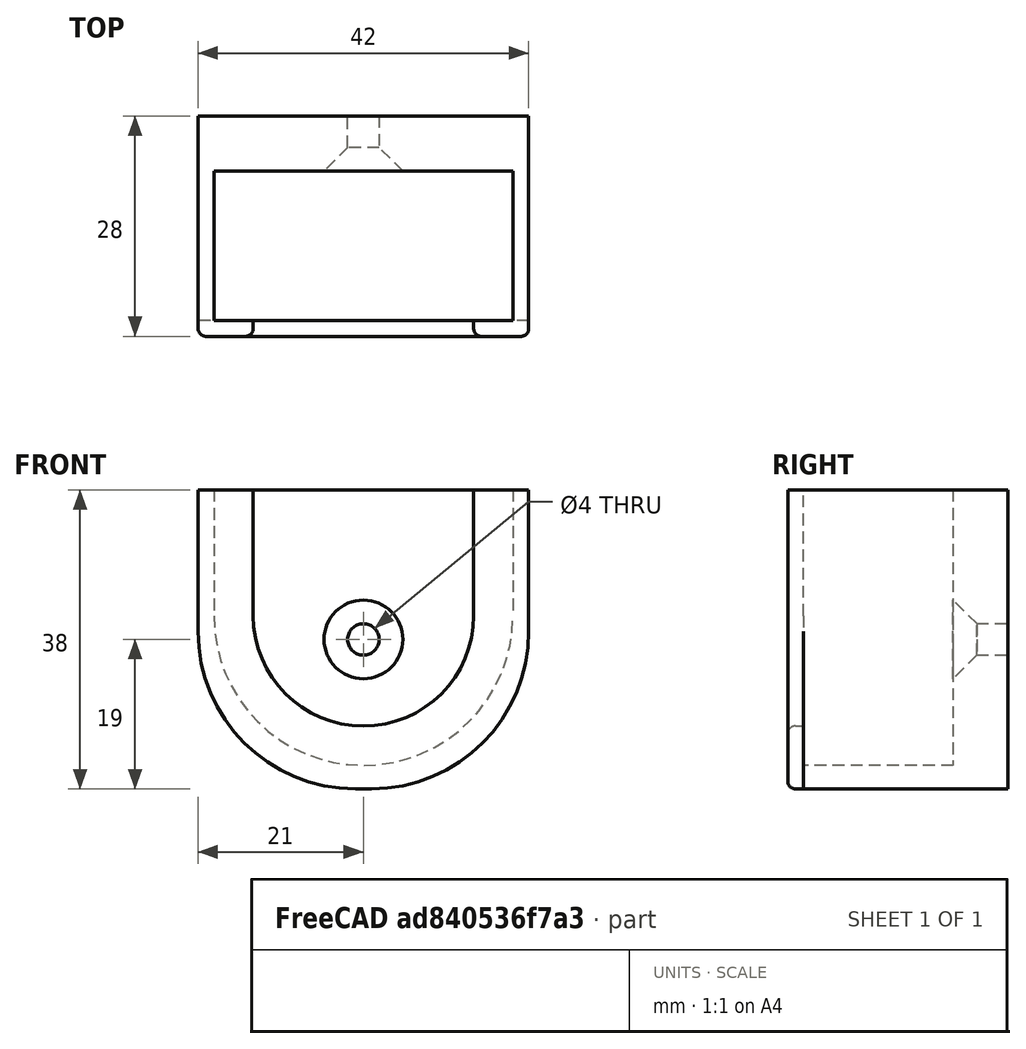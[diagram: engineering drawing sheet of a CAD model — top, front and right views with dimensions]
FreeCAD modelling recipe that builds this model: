
FCSTD DOCUMENT  (FreeCAD 0.19R24291 (Git))
Label: 003
License: All rights reserved
LicenseURL: http://en.wikipedia.org/wiki/All_rights_reserved
objects: PartDesign::Fillet×6, Sketcher::SketchObject×5, PartDesign::Pocket×3, PartDesign::Pad×2, PartDesign::Plane×1, PartDesign::Chamfer×1, PartDesign::Body×1
note: 31 computed .brp shape members not serialized (recipe doc carries the construction recipe); baked Part::Feature solids carry a one-line shape summary decoded from their .brp

FEATURE [Sketcher::SketchObject] Sketch
  FullyConstrained = true
  MapMode = 5
  Placement = pos=(0,0,0) rot=(1,0,0;1.5708rad)
  Support = -> [XZ_Plane]
  sketch-geometry (4):
    g0: LineSegment StartX=0 StartY=38 StartZ=0 EndX=42 EndY=38 EndZ=0
    g1: LineSegment StartX=42 StartY=38 StartZ=0 EndX=42 EndY=0 EndZ=0
    g2: LineSegment StartX=42 StartY=0 StartZ=0 EndX=0 EndY=0 EndZ=0
    g3: LineSegment StartX=0 StartY=0 StartZ=0 EndX=0 EndY=38 EndZ=0
  constraints (11):
    c: Coincident(g0,g1)
    c: Coincident(g1,g2)
    c: Coincident(g2,g3)
    c: Coincident(g3,g0)
    c: Horizontal(g0)
    c: Horizontal(g2)
    c: Vertical(g1)
    c: Vertical(g3)
    c: DistanceX(g0,g0) = 42
    c: DistanceY(g1,g1) = 38
    c: Coincident(g-1,g2)
FEATURE [PartDesign::Pad] Pad
  Direction = (1,1,1)
  Length = 26
  Length2 = 100
  Placement = pos=(0,0,0) rot=(1,0,0;1.5708rad)
  Profile = -> Sketch
  Type = 0
FEATURE [Sketcher::SketchObject] Sketch001
  ExternalGeometry = -> [Pad]
  FullyConstrained = true
  MapMode = 5
  Placement = pos=(0,-26,-5.8e-15) rot=(1,0,0;1.5708rad)
  Support = -> [Pad]
  sketch-geometry (4):
    g0: ArcOfCircle CenterX=21 CenterY=38 CenterZ=0 NormalX=0 NormalY=0 NormalZ=1 AngleXU=0 Radius=19 StartAngle=2e-16 EndAngle=3.14159
    g1: ArcOfCircle CenterX=21 CenterY=22 CenterZ=0 NormalX=0 NormalY=0 NormalZ=1 AngleXU=0 Radius=19 StartAngle=3.14159 EndAngle=6.28319
    g2: LineSegment StartX=2 StartY=38 StartZ=0 EndX=2 EndY=22 EndZ=0
    g3: LineSegment StartX=40 StartY=38 StartZ=0 EndX=40 EndY=22 EndZ=0
  constraints (9):
    c: Tangent(g0,g3) = 1.5708
    c: Tangent(g0,g2) = -1.5708
    c: Tangent(g2,g1) = -1.5708
    c: Tangent(g3,g1) = 1.5708
    c: Vertical(g2)
    c: Equal(g0,g1)
    c: DistanceX(g0,g0) = 38
    c: Symmetric(g-3,g-4,g0)
    c: DistanceY(g2,g2) = 16
FEATURE [PartDesign::Pocket] Pocket
  BaseFeature = -> Pad
  Length = 19
  Length2 = 100
  Placement = pos=(0,0,0) rot=(1,0,0;1.5708rad)
  Profile = -> Sketch001
  Refine = true
  Type = 0
FEATURE [PartDesign::Plane] DatumPlane
  Length = 79.9938
  MapMode = 5
  Placement = pos=(0,-26,-5.8e-15) rot=(1,0,0;1.5708rad)
  ResizeMode = 0
  Support = -> [Pocket]
  Width = 75.9938
FEATURE [Sketcher::SketchObject] Sketch002
  ExternalGeometry = -> [Pocket]
  FullyConstrained = false
  MapMode = 5
  Placement = pos=(0,-26,-5.8e-15) rot=(1,0,0;1.5708rad)
  Support = -> [DatumPlane]
  sketch-geometry (4):
    g0: ArcOfCircle CenterX=21 CenterY=22 CenterZ=0 NormalX=0 NormalY=0 NormalZ=1 AngleXU=0 Radius=14 StartAngle=3.14159 EndAngle=6.28319
    g1: ArcOfCircle CenterX=21 CenterY=40.6173 CenterZ=0 NormalX=0 NormalY=0 NormalZ=1 AngleXU=0 Radius=14 StartAngle=0 EndAngle=3.14159
    g2: LineSegment StartX=35 StartY=22 StartZ=0 EndX=35 EndY=40.6173 EndZ=0
    g3: LineSegment StartX=7 StartY=22 StartZ=0 EndX=7 EndY=40.6173 EndZ=0
  constraints (8):
    c: Tangent(g0,g3) = 1.5708
    c: Tangent(g0,g2) = -1.5708
    c: Tangent(g2,g1) = -1.5708
    c: Tangent(g3,g1) = 1.5708
    c: Vertical(g2)
    c: Equal(g0,g1)
    c: Coincident(g0,g-3)
    c: DistanceX(g0,g-4) = 5
FEATURE [PartDesign::Fillet] Fillet
  Base = -> Pocket [Edge24,Edge12]
  BaseFeature = -> Pocket
  Placement = pos=(0,0,0) rot=(1,0,0;1.5708rad)
  Radius = 20
  SupportTransform = false
FEATURE [Sketcher::SketchObject] Sketch003
  ExternalGeometry = -> [Fillet]
  FullyConstrained = true
  MapMode = 5
  Placement = pos=(0,-26,-5.8e-15) rot=(1,0,0;1.5708rad)
  Support = -> [DatumPlane]
  sketch-geometry (4):
    g0: LineSegment StartX=0 StartY=38 StartZ=0 EndX=42 EndY=38 EndZ=0
    g1: LineSegment StartX=42 StartY=38 StartZ=0 EndX=42 EndY=0 EndZ=0
    g2: LineSegment StartX=42 StartY=0 StartZ=0 EndX=0 EndY=0 EndZ=0
    g3: LineSegment StartX=0 StartY=0 StartZ=0 EndX=0 EndY=38 EndZ=0
  constraints (9):
    c: Coincident(g0,g1)
    c: Coincident(g1,g2)
    c: Coincident(g2,g3)
    c: Coincident(g3,g0)
    c: Horizontal(g2)
    c: Vertical(g1)
    c: Coincident(g0,g-4)
    c: Coincident(g0,g-3)
    c: Coincident(g2,g-1)
FEATURE [PartDesign::Pad] Pad001
  BaseFeature = -> Fillet
  Direction = (1,1,1)
  Length = 2
  Length2 = 100
  Placement = pos=(0,0,0) rot=(1,0,0;1.5708rad)
  Profile = -> Sketch003
  Type = 0
FEATURE [PartDesign::Pocket] Pocket001
  BaseFeature = -> Pad001
  Length = 5
  Length2 = 100
  Placement = pos=(0,0,0) rot=(1,0,0;1.5708rad)
  Profile = -> Sketch002
  Reversed = true
  Type = 0
FEATURE [PartDesign::Fillet] Fillet001
  Base = -> Pocket001 [Edge24]
  BaseFeature = -> Pocket001
  Placement = pos=(0,0,0) rot=(1,0,0;1.5708rad)
  Radius = 20
  SupportTransform = false
FEATURE [PartDesign::Fillet] Fillet002
  Base = -> Fillet001 [Edge21]
  BaseFeature = -> Fillet001
  Placement = pos=(0,0,0) rot=(1,0,0;1.5708rad)
  Radius = 20
  SupportTransform = false
FEATURE [Sketcher::SketchObject] Sketch004
  ExternalGeometry = -> [Fillet002]
  FullyConstrained = true
  MapMode = 5
  Placement = pos=(0,0,0) rot=(-1,0,0;1.5708rad)
  Support = -> [Fillet002]
  sketch-geometry (1):
    g0: Circle CenterX=21 CenterY=-19 CenterZ=0 NormalX=0 NormalY=0 NormalZ=1 AngleXU=0 Radius=2
  constraints (2):
    c: Symmetric(g-3,g-1,g0)
    c: Radius(g0) = 2
FEATURE [PartDesign::Pocket] Pocket002
  BaseFeature = -> Fillet002
  Length = 10
  Length2 = 100
  Placement = pos=(0,0,0) rot=(1,0,0;1.5708rad)
  Profile = -> Sketch004
  Type = 0
FEATURE [PartDesign::Chamfer] Chamfer
  Angle = 45
  Base = -> Pocket002 [Edge58]
  BaseFeature = -> Pocket002
  ChamferType = 0
  FlipDirection = false
  Placement = pos=(0,0,0) rot=(1,0,0;1.5708rad)
  Size = 3
  Size2 = 1
  SupportTransform = false
FEATURE [PartDesign::Fillet] Fillet003
  Base = -> Chamfer [Edge52,Edge57]
  BaseFeature = -> Chamfer
  Placement = pos=(0,0,0) rot=(1,0,0;1.5708rad)
  Radius = 1
  SupportTransform = false
FEATURE [PartDesign::Fillet] Fillet004
  Base = -> Fillet003 [Edge23]
  BaseFeature = -> Fillet003
  Placement = pos=(0,0,0) rot=(1,0,0;1.5708rad)
  Radius = 1
  SupportTransform = false
FEATURE [PartDesign::Fillet] Fillet005
  Base = -> Fillet004 [Edge33]
  BaseFeature = -> Fillet004
  Placement = pos=(0,0,0) rot=(1,0,0;1.5708rad)
  Radius = 1
  SupportTransform = false
FEATURE [PartDesign::Body] Body
  Group = -> [Sketch,Pad,Sketch001,Pocket,DatumPlane,Sketch002,Fillet,Sketch003,Pad001,Pocket001,Fillet001,Fillet002,Sketch004,Pocket002,Chamfer,Fillet003,Fillet004,Fillet005]
  Origin = -> Origin
  Tip = -> Fillet005
